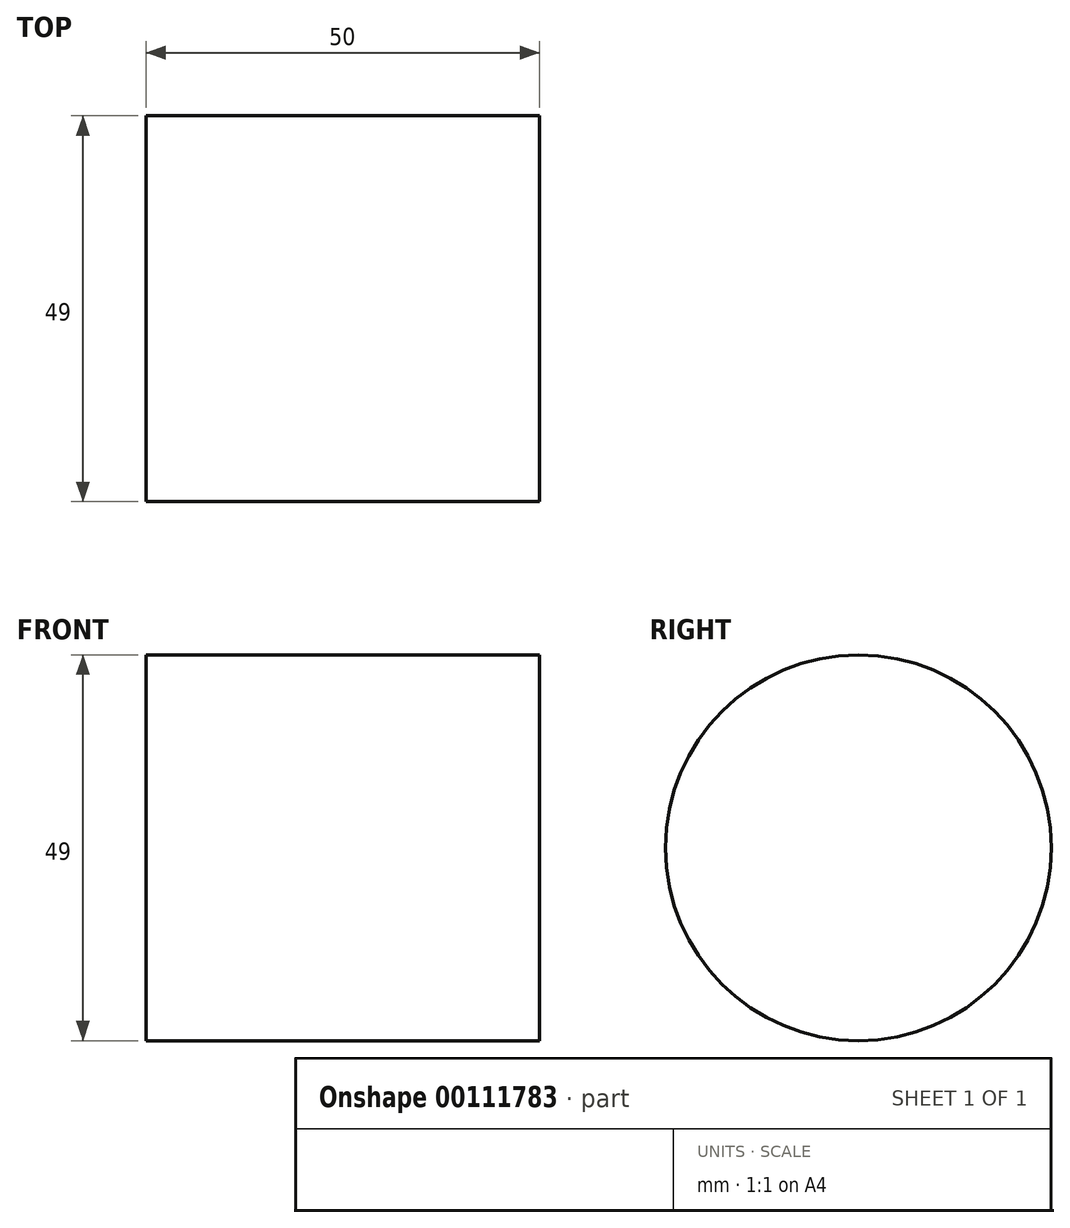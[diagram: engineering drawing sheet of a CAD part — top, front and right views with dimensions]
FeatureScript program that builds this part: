
annotation { "Feature Type Name" : "Feature", "Feature Type Description" : "" }
export const myFeature = defineFeature(function(context is Context, id is Id, definition is map)
    precondition{}
    {
        {
            var Q0;
            Q0=qCreatedBy(makeId("Right.planeOp"),FACE);
            var sketch = newSketch(context, id + "F0", { "sketchPlane" : qUnion([Q0])});
            skCircle(sketch, "E0", {"center": v(0, 0) * mm, "radius": 24.5 * mm});
            skSolve(sketch);
        }
        {
            var Q0;
            Q0=makeQuery(id+"F0.imprint","IMPRINT",FACE,{"disambiguationData":[TD([[makeQuery(id+"F0.imprint","IMPRINT",EDGE,{"derivedFrom":sQuery(id+"F0.wireOp",EDGE,"E0")}),1.0]])]});
            var Q1;
            Q1=sQuery(id+"F0.wireOp",EDGE,"E0");
            extrude(context, id + "F1", {"entities" : qUnion([Q0]), "surfaceEntities" : qUnion([Q1]), "depth" : 50 * mm});
        }
    });
